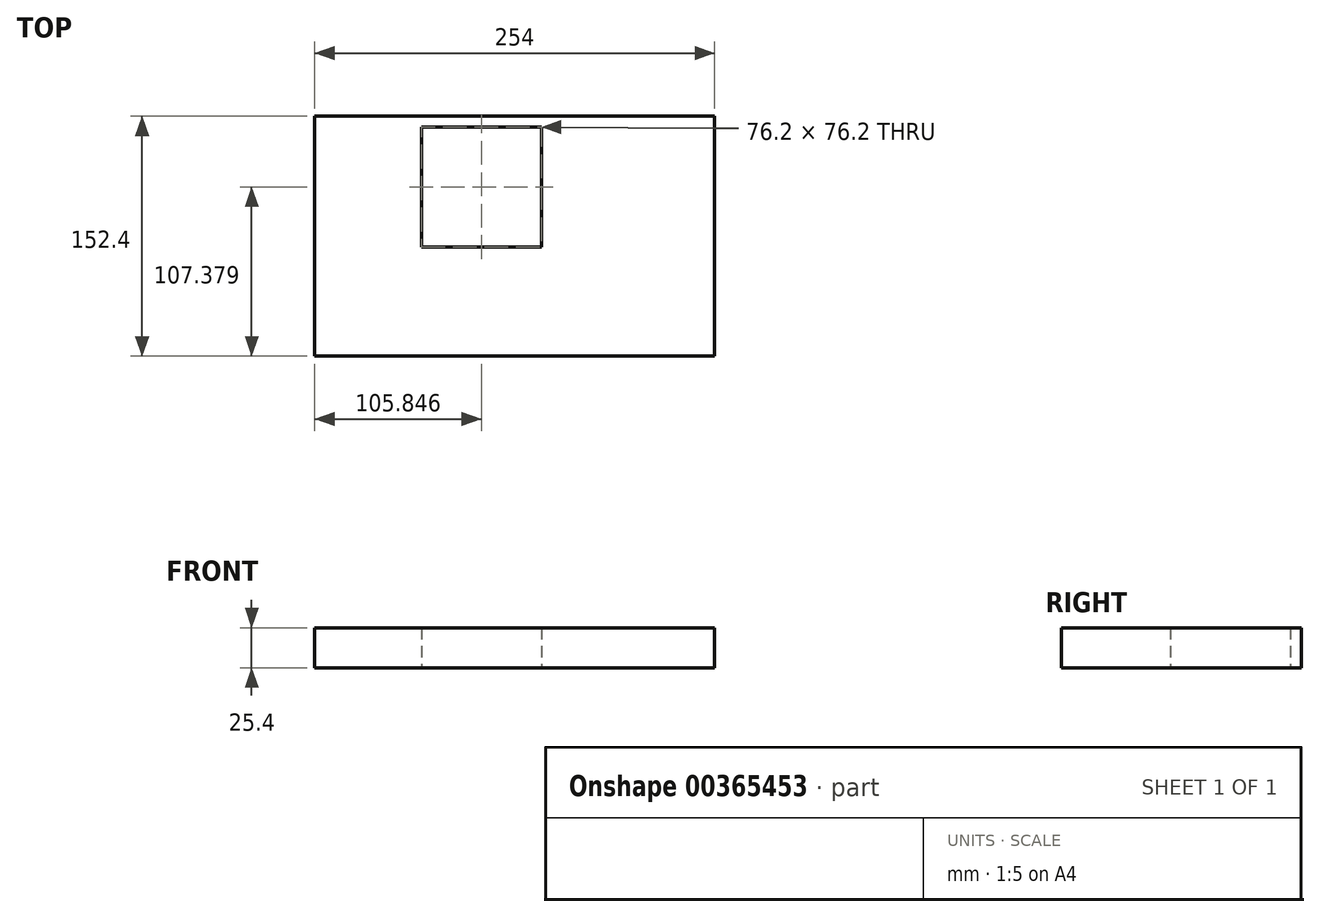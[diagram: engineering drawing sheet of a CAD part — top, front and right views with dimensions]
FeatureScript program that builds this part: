
annotation { "Feature Type Name" : "Feature", "Feature Type Description" : "" }
export const myFeature = defineFeature(function(context is Context, id is Id, definition is map)
    precondition{}
    {
        {
            var Q0;
            Q0=qCreatedBy(makeId("Top.planeOp"),FACE);
            var sketch = newSketch(context, id + "F0", { "sketchPlane" : qUnion([Q0])});
            skLineSegment(sketch, "E0.bottom", {"start": v(-127, 76.2) * mm, "end": v(127, 76.2) * mm});
            skLineSegment(sketch, "E0.top", {"start": v(-127, -76.2) * mm, "end": v(127, -76.2) * mm});
            skLineSegment(sketch, "E0.left", {"start": v(-127, 76.2) * mm, "end": v(-127, -76.2) * mm});
            skLineSegment(sketch, "E0.right", {"start": v(127, 76.2) * mm, "end": v(127, -76.2) * mm});
            skPoint(sketch, "E0.middle", {"position": v(0, 0) * mm});
            skLineSegment(sketch, "E1.bottom", {"start": v(-59.25, 69.28) * mm, "end": v(16.95, 69.28) * mm});
            skLineSegment(sketch, "E1.top", {"start": v(-59.25, -6.92) * mm, "end": v(16.95, -6.92) * mm});
            skLineSegment(sketch, "E1.left", {"start": v(-59.25, 69.28) * mm, "end": v(-59.25, -6.92) * mm});
            skLineSegment(sketch, "E1.right", {"start": v(16.95, 69.28) * mm, "end": v(16.95, -6.92) * mm});
            skPoint(sketch, "E1.middle", {"position": v(-21.15, 31.18) * mm});
            skSolve(sketch);
        }
        {
            var Q0;
            Q0 = qSketchRegion(id + "F0", true);
            extrude(context, id + "F1", {"entities" : qUnion([Q0]), "depth" : 25.4 * mm});
        }
    });
